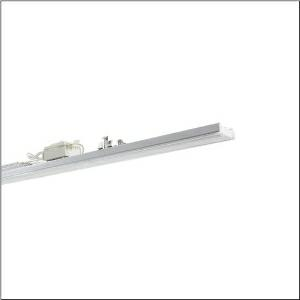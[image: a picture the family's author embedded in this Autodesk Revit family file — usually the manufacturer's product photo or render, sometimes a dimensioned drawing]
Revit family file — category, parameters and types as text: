
# Revit family: licross_r__21_recessed_mo_52tl11dn48xg_7dee
name_source: partatom
category: Lighting Fixtures
units: mm (PartAtom-declared; Revit-internal decimal feet)

## family parameters
Cut with Voids When Loaded = No
Host = Face
Light Source = No
Part Type = Normal
Room Calculation Point = No
Round Connector Dimension = Use Diameter
Shared = No

## types (1)
- --- (1 x LED, 8000 lm, 45 W, 4000K)
    Apparent Load = 45 VA
    CIE Flux Codes = 89 96 99 100 100
    Color Rendering = 80
    Color Temperature = 4000K
    Default Elevation = 1800 mm
    Description = Licross® 21 Recessed MO, luminaire insert, of sheet steel, galvanised, coil coated, white, length: 1.500mm, width: 66mm, height: 67mm, LED rated luminous flux: 8.000lm, light colour: 840, control gear: DALI 2, with plug, 5-pole, with phase selection, mains connection: 220..240V, AC, 50/60Hz, rated input power: 45W, internal wiring halogen-free, primary light control with lens, of plastic, primary optical cover: cover, of PMMA, light emission: direct distribution, primary light characteristic: symmetric, protection rating (complete): IP40, insulation class (complete): insulation class I (protective earthing), certification: CE, ENEC, VDE, UKCA, protection symbol: D if used in an environment without relevant dust loads with corresponding accessories, impact resistance: IK06, permissible ambient temperature for indoor applications: -25..+35°C, corresponds to IFS (International Featured Standards) requirements for safety and quality in the food industry, reducing of maximum allowable ambient temperature of 5°C with ceiling mounting, LABS conformity tested according to VDMA 24364:2018-05, packaging unit: 1 piece
    Height = 58 mm
    Lamp = 1 x LED
    Lamp Light Flux = 8000 lm
    Lamp Power = 45 W
    Lamp count = 1
    Length = 1500 mm
    Luminous efficacy = 178 lm/W
    Manufacturer = Siteco
    ModVariant = No
    Model = 52TL11DN48XG
    Mounting Place = Ceiling
    Mounting Type = Pendant
    Number of Poles = 1
    OnlyDefault = Yes
    Power Factor = 1
    Product Name = Licross® 21 Recessed MO
    Product group = luminaire insert | ceiling pendant
    ProductGroupID = 902
    Protection Class = Protection class I
    Protection Degree = IP 40
    RLX_Detail_Level = 1
    RLX_Emergency_Light_Flux = 0 lm
    RLX_Emergency_Type = 0
    RLX_Emergency_Type_DB = No
    RlxData = <blob elided: 24553 chars, md5=23c7adf1>
    Socket = socket
    Standby Power = 0 W
    System Light Flux = 8000 lm
    System Power = 45 W
    Type Comments = factory setting: luminous flux: 100 % | dim-lin: 254 | 302 mA
    Type Image = l_1296930.jpg
    URL = http://relux.com
    VarID = @adj_148369
    Voltage = 0 V
    Weight = 0.00 kg
    Width = 66 mm

## geometry (parser evidence)
native form markers: Blend x4, Sweep x11
no freeform markers — native parametric forms only
